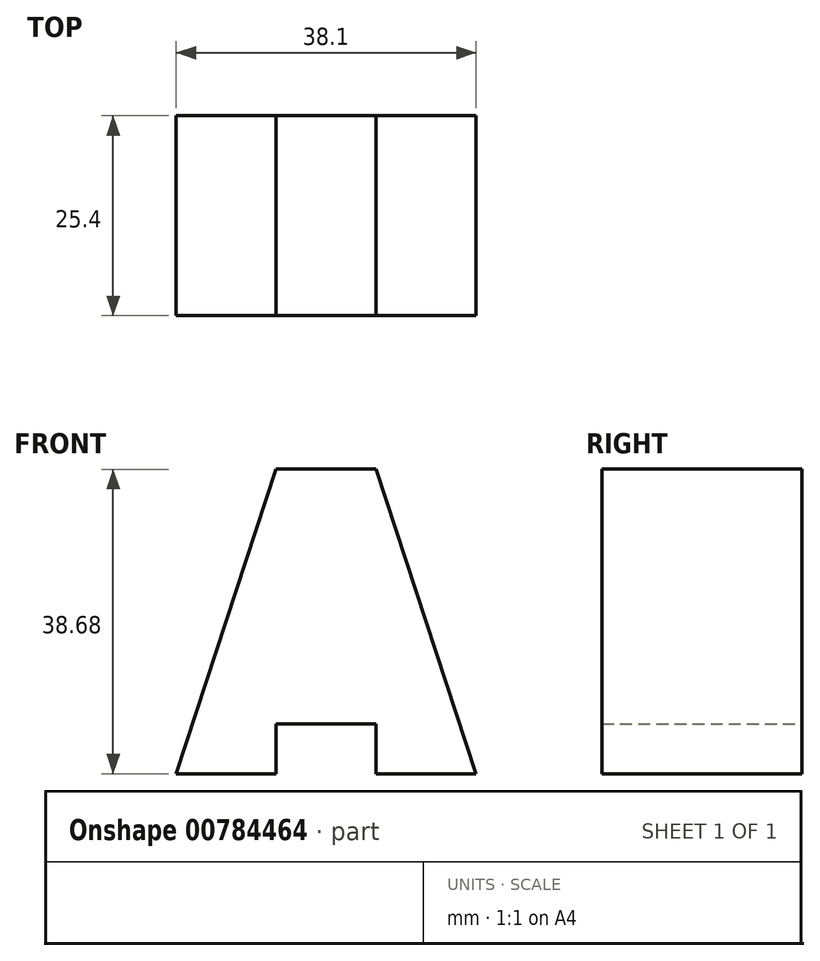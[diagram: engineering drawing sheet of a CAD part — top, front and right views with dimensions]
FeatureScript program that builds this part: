
annotation { "Feature Type Name" : "Feature", "Feature Type Description" : "" }
export const myFeature = defineFeature(function(context is Context, id is Id, definition is map)
    precondition{}
    {
        {
            var Q0;
            Q0=qCreatedBy(makeId("Front.planeOp"),FACE);
            var sketch = newSketch(context, id + "F0", { "sketchPlane" : qUnion([Q0])});
            skLineSegment(sketch, "E0", {"start": v(0, 0) * mm, "end": v(12.7, 0) * mm});
            skLineSegment(sketch, "E1", {"start": v(12.7, 0) * mm, "end": v(12.7, 6.35) * mm});
            skLineSegment(sketch, "E2", {"start": v(12.7, 6.35) * mm, "end": v(25.4, 6.35) * mm});
            skLineSegment(sketch, "E3", {"start": v(25.4, 6.35) * mm, "end": v(25.4, 0) * mm});
            skLineSegment(sketch, "E4", {"start": v(25.4, 0) * mm, "end": v(38.1, 0) * mm});
            skLineSegment(sketch, "E5", {"start": v(0, 0) * mm, "end": v(12.7, 38.68) * mm});
            skLineSegment(sketch, "E6", {"start": v(12.7, 38.68) * mm, "end": v(25.4, 38.68) * mm});
            skLineSegment(sketch, "E7", {"start": v(25.4, 38.68) * mm, "end": v(38.1, 0) * mm});
            skSolve(sketch);
        }
        {
            var Q0;
            Q0=makeQuery(id+"F0.imprint","IMPRINT",FACE,{"disambiguationData":[TD([[makeQuery(id+"F0.imprint","IMPRINT",EDGE,{"derivedFrom":sQuery(id+"F0.wireOp",EDGE,"E0")}),1.0]])]});
            extrude(context, id + "F1", {"entities" : qUnion([Q0]), "depth" : 25.4 * mm, "offsetDistance" : 25.4 * mm});
        }
    });
